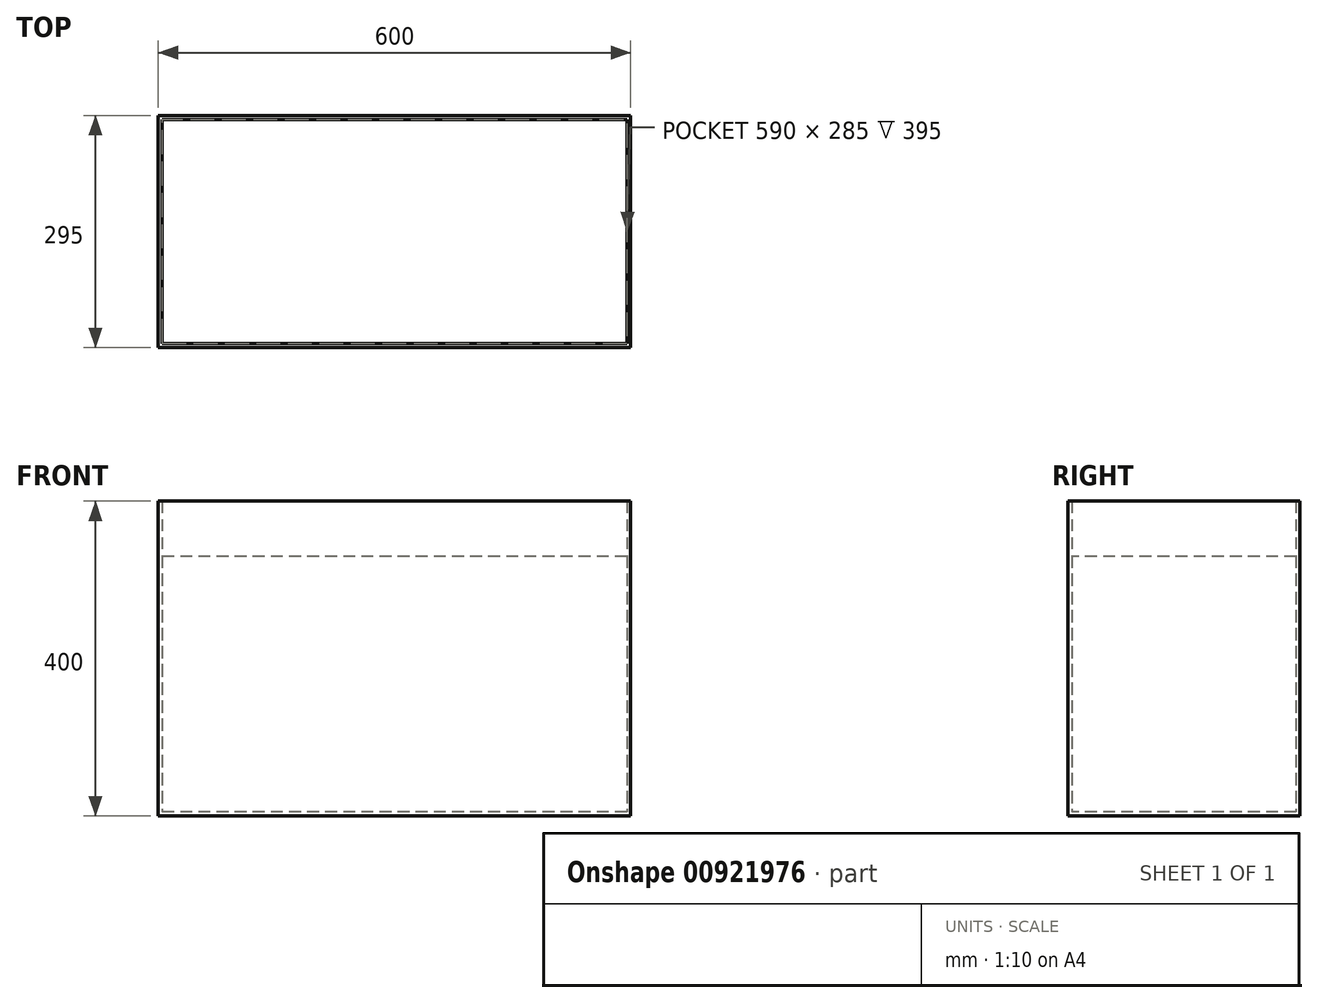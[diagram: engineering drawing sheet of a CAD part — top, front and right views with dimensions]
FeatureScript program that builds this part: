
annotation { "Feature Type Name" : "Feature", "Feature Type Description" : "" }
export const myFeature = defineFeature(function(context is Context, id is Id, definition is map)
    precondition{}
    {
        {
            var Q0;
            Q0=qCreatedBy(makeId("Top.planeOp"),FACE);
            var sketch = newSketch(context, id + "F0", { "sketchPlane" : qUnion([Q0])});
            skLineSegment(sketch, "E0.bottom", {"start": v(300, 147.5) * mm, "end": v(-300, 147.5) * mm});
            skLineSegment(sketch, "E0.top", {"start": v(300, -147.5) * mm, "end": v(-300, -147.5) * mm});
            skLineSegment(sketch, "E0.left", {"start": v(300, 147.5) * mm, "end": v(300, -147.5) * mm});
            skLineSegment(sketch, "E0.right", {"start": v(-300, 147.5) * mm, "end": v(-300, -147.5) * mm});
            skPoint(sketch, "E0.middle", {"position": v(0, 0) * mm});
            skSolve(sketch);
        }
        {
            var Q0;
            Q0=makeQuery(id+"F0.imprint","IMPRINT",FACE,{"disambiguationData":[TD([[makeQuery(id+"F0.imprint","IMPRINT",EDGE,{"derivedFrom":sQuery(id+"F0.wireOp",EDGE,"E0.bottom")}),1.0]])]});
            extrude(context, id + "F1", {"entities" : qUnion([Q0]), "depth" : 400 * mm, "offsetDistance" : 25 * mm});
        }
        {
            var Q0;
            Q0=makeQuery(id+"F1.opExtrude","CAP_FACE",FACE,{"disambiguationData":[OSD([sQuery(id+"F0.wireOp",EDGE,"E0.bottom"),sQuery(id+"F0.wireOp",EDGE,"E0.top"),sQuery(id+"F0.wireOp",EDGE,"E0.left"),sQuery(id+"F0.wireOp",EDGE,"E0.right")])],"isStart":false});
            shell(context, id + "F2", {"entities" : qUnion([Q0]), "thickness" : 5 * mm});
        }
        {
            var Q0;
            Q0=makeQuery(id+"F2.opShell","OFFSET_FACE",FACE,{"disambiguationData":[OSD([sQuery(id+"F0.wireOp",EDGE,"E0.bottom"),sQuery(id+"F0.wireOp",EDGE,"E0.top"),sQuery(id+"F0.wireOp",EDGE,"E0.left"),sQuery(id+"F0.wireOp",EDGE,"E0.right")])]});
            var sketch = newSketch(context, id + "F3", { "sketchPlane" : qUnion([Q0])});
            skSolve(sketch);
        }
        {
            var Q0;
            Q0=qSketchRegion(id+"F3",true);
            var Q1;
            {var subQ0=sQuery(id+"F0.wireOp",EDGE,"E0.bottom");Q1=makeQuery(id+"F3.imprint","IMPRINT",FACE,{"disambiguationData":[TD([[makeQuery(id+"F3.imprint","IMPRINT",EDGE,{"derivedFrom":makeQuery(id+"F2.opShell","OFFSET_EDGE",EDGE,{"disambiguationData":[OSD([subQ0]),TDD([makeQuery(id+"F1.opExtrude","CAP_EDGE",EDGE,{"disambiguationData":[OSD([subQ0])],"isStart":true})])]})}),1.0]])]});}
            extrude(context, id + "F4", {"entities" : qUnion([Q0, Q1]), "depth" : 325 * mm, "offsetDistance" : 25 * mm});
        }
    });
